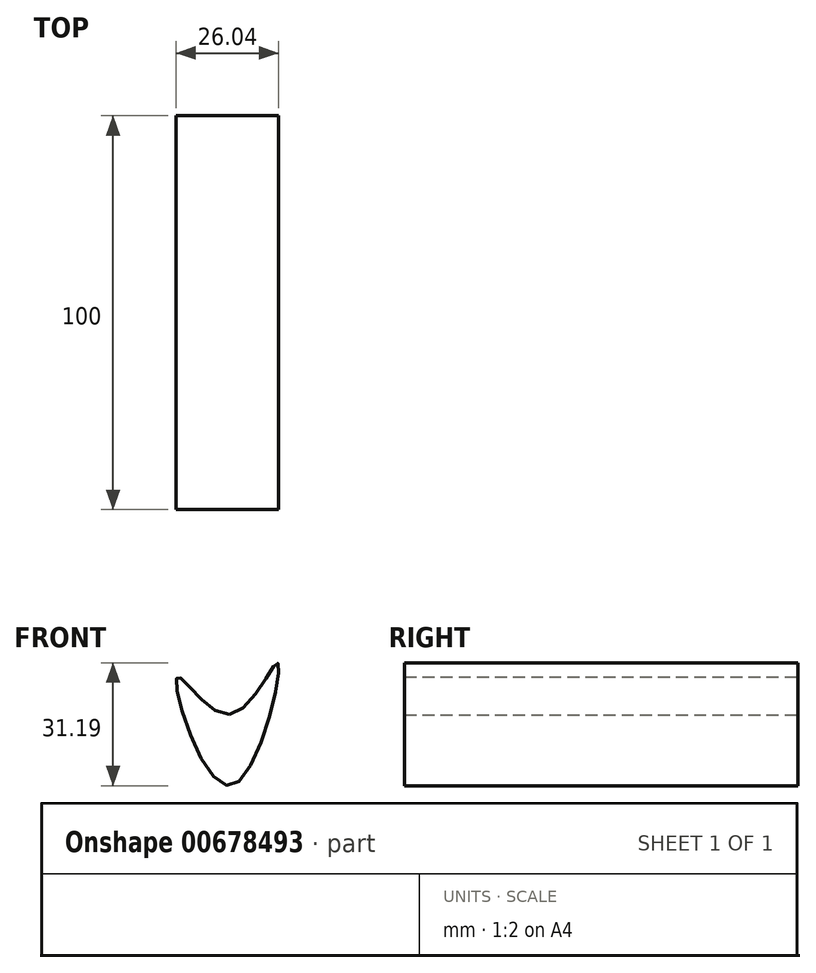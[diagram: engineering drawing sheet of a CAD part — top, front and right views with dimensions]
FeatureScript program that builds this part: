
annotation { "Feature Type Name" : "Feature", "Feature Type Description" : "" }
export const myFeature = defineFeature(function(context is Context, id is Id, definition is map)
    precondition{}
    {
        {
            var Q0;
            Q0=qCreatedBy(makeId("Front.planeOp"),FACE);
            var sketch = newSketch(context, id + "F0", { "sketchPlane" : qUnion([Q0])});
            skFitSpline(sketch, "E0", {"points": [v(-0.1, 1.2) * mm, v(12.16, 14.28) * mm, v(-0.1, -16.83) * mm, v(-13.45, 10.7) * mm, v(-0.1, 1.2) * mm]});
            skCircle(sketch, "E1.cCircle", {"center": v(0, 0) * mm, "radius": 24.47 * mm, "construction": true});
            skLineSegment(sketch, "E1.0", {"start": v(-12.22, 21.2) * mm, "end": v(12.25, 21.18) * mm});
            skLineSegment(sketch, "E1.1", {"start": v(12.25, 21.18) * mm, "end": v(24.47, -0.02) * mm});
            skLineSegment(sketch, "E1.2", {"start": v(24.47, -0.02) * mm, "end": v(12.22, -21.2) * mm});
            skLineSegment(sketch, "E1.3", {"start": v(12.22, -21.2) * mm, "end": v(-12.25, -21.18) * mm});
            skLineSegment(sketch, "E1.4", {"start": v(-12.25, -21.18) * mm, "end": v(-24.47, 0.02) * mm});
            skLineSegment(sketch, "E1.5", {"start": v(-24.47, 0.02) * mm, "end": v(-12.22, 21.2) * mm});
            skSolve(sketch);
        }
        {
            var Q0;
            Q0=makeQuery(id+"F0.imprint","IMPRINT",FACE,{"disambiguationData":[TD([[makeQuery(id+"F0.imprint","IMPRINT",EDGE,{"derivedFrom":sQuery(id+"F0.wireOp",EDGE,"E0")}),-1.0]])]});
            extrude(context, id + "F1", {"entities" : qUnion([Q0]), "depth" : 100 * mm, "offsetDistance" : 25 * mm});
        }
    });
